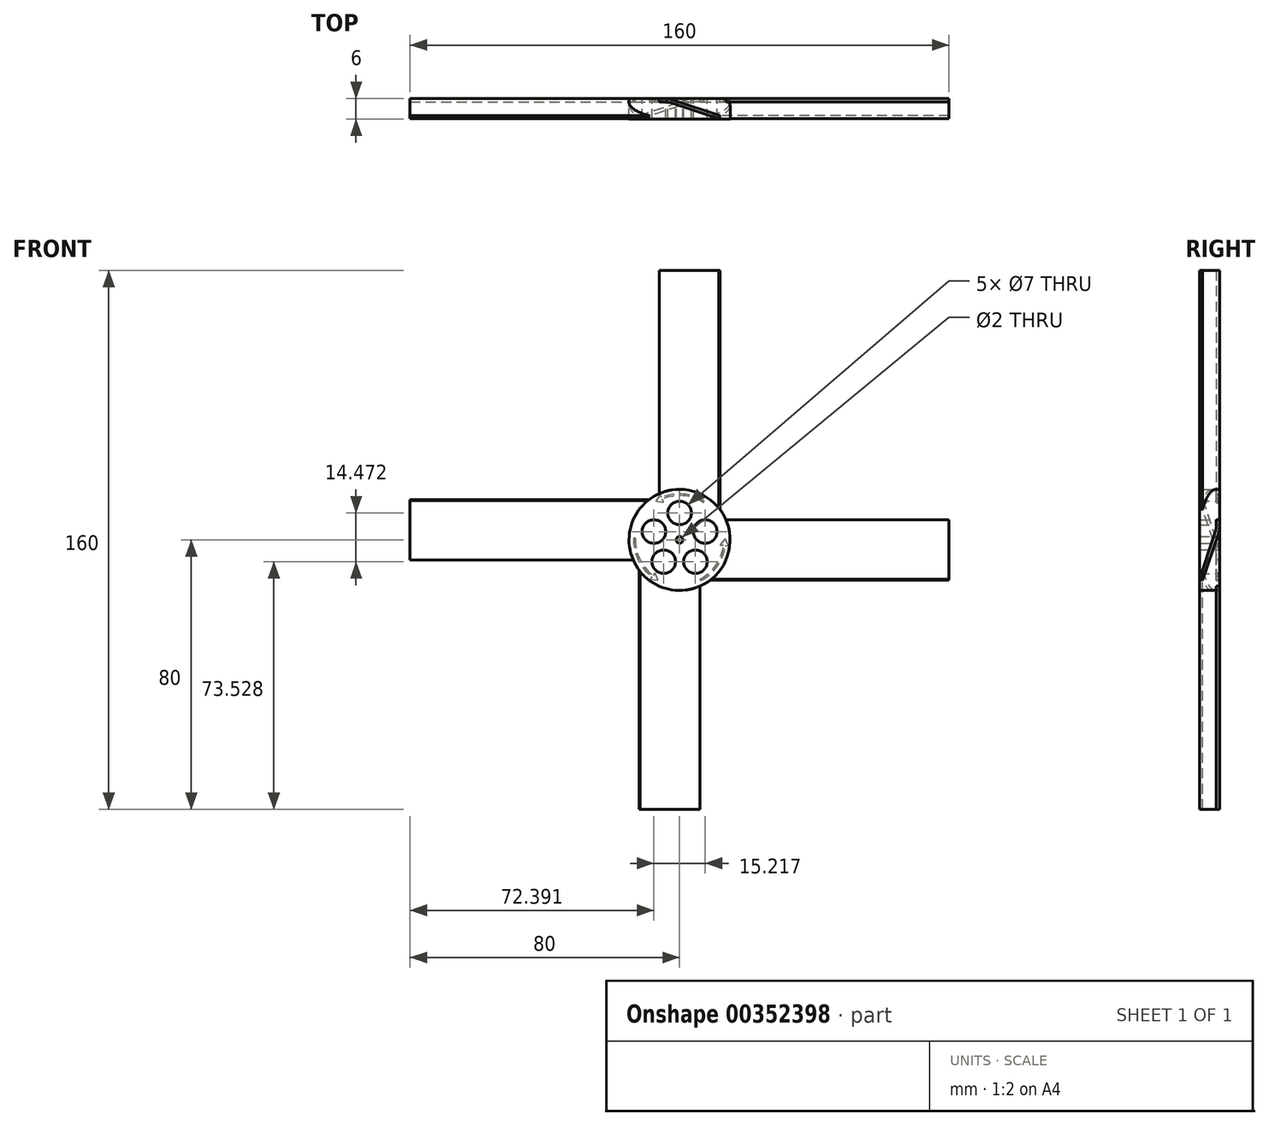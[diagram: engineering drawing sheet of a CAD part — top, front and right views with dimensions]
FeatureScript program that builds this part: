
annotation { "Feature Type Name" : "Feature", "Feature Type Description" : "" }
export const myFeature = defineFeature(function(context is Context, id is Id, definition is map)
    precondition{}
    {
        {
            var Q0;
            Q0=qCreatedBy(makeId("Top.planeOp"),FACE);
            var sketch = newSketch(context, id + "F0", { "sketchPlane" : qUnion([Q0])});
            skLineSegment(sketch, "E0", {"start": v(-3, 0) * mm, "end": v(12, 0) * mm, "construction": true});
            skLineSegment(sketch, "E1", {"start": v(12, 0) * mm, "end": v(12, -5) * mm, "construction": true});
            skLineSegment(sketch, "E2", {"start": v(12, -5) * mm, "end": v(-3, 0) * mm});
            skLineSegment(sketch, "E3.0", {"start": v(11.68, -5.95) * mm, "end": v(-3.32, -0.95) * mm});
            skLineSegment(sketch, "E4", {"start": v(11.68, -5.95) * mm, "end": v(12, -5) * mm});
            skLineSegment(sketch, "E5", {"start": v(-3, 0) * mm, "end": v(-3.32, -0.95) * mm});
            skLineSegment(sketch, "E6", {"start": v(-3, 0) * mm, "end": v(-6, 0) * mm});
            skLineSegment(sketch, "E7", {"start": v(-6, 0) * mm, "end": v(-6, -0.95) * mm});
            skLineSegment(sketch, "E8", {"start": v(-6, -0.95) * mm, "end": v(-3.32, -0.95) * mm});
            skSolve(sketch);
        }
        {
            var Q0;
            Q0=makeQuery(id+"F0.imprint","IMPRINT",FACE,{"disambiguationData":[TD([[makeQuery(id+"F0.imprint","IMPRINT",EDGE,{"derivedFrom":sQuery(id+"F0.wireOp",EDGE,"E2")}),1.0]])]});
            var Q1;
            Q1=makeQuery(id+"F0.imprint","IMPRINT",FACE,{"disambiguationData":[TD([[makeQuery(id+"F0.imprint","IMPRINT",EDGE,{"derivedFrom":sQuery(id+"F0.wireOp",EDGE,"E5")}),-1.0]])]});
            extrude(context, id + "F1", {"entities" : qUnion([Q0, Q1]), "oppositeDirection" : true, "depth" : 80 * mm});
        }
        {
            var Q0;
            Q0=makeQuery(id+"F1.opExtrude","SWEPT_EDGE",EDGE,{"disambiguationData":[OSD([sQuery(id+"F0.wireOp",EDGE,"E3.0"),sQuery(id+"F0.wireOp",EDGE,"E5"),sQuery(id+"F0.wireOp",EDGE,"E8")])]});
            var Q1;
            Q1=makeQuery(id+"F1.opExtrude","SWEPT_EDGE",EDGE,{"disambiguationData":[OSD([sQuery(id+"F0.wireOp",EDGE,"E2"),sQuery(id+"F0.wireOp",EDGE,"E5"),sQuery(id+"F0.wireOp",EDGE,"E6")])]});
            fillet(context, id + "F2", {"entities" : qUnion([Q0, Q1]), "radius" : 7.64 * mm, "tangentPropagation" : true, "allowEdgeOverflow" : false});
        }
        {
            var Q0;
            Q0=qCreatedBy(makeId("Top.planeOp"),FACE);
            var sketch = newSketch(context, id + "F3", { "sketchPlane" : qUnion([Q0])});
            skLineSegment(sketch, "E9", {"start": v(0, 0) * mm, "end": v(0, 27.05) * mm, "construction": true});
            skSolve(sketch);
        }
        {
            var Q0;
            Q0=makeQuery(id+"F1.opExtrude","SWEPT_BODY",BODY,{"disambiguationData":[OSD([sQuery(id+"F0.wireOp",EDGE,"E2"),sQuery(id+"F0.wireOp",EDGE,"E3.0"),sQuery(id+"F0.wireOp",EDGE,"E4"),sQuery(id+"F0.wireOp",EDGE,"E5")])]});
            var Q1;
            Q1=sQuery(id+"F3.wireOp",EDGE,"E9");
            circularPattern(context, id + "F4", {"entities" : qUnion([Q0]), "axis" : qUnion([Q1]), "angle" : 360 * degree, "instanceCount" : 4, "equalSpace" : true});
        }
        {
            var Q0;
            Q0=qCreatedBy(makeId("Front.planeOp"),FACE);
            var sketch = newSketch(context, id + "F5", { "sketchPlane" : qUnion([Q0])});
            skCircle(sketch, "E10", {"center": v(0, 0) * mm, "radius": 15 * mm});
            skSolve(sketch);
        }
        {
            var Q0;
            Q0=makeQuery(id+"F5.imprint","IMPRINT",FACE,{"disambiguationData":[TD([[makeQuery(id+"F5.imprint","IMPRINT",EDGE,{"derivedFrom":sQuery(id+"F5.wireOp",EDGE,"E10")}),1.0]])]});
            extrude(context, id + "F6", {"entities" : qUnion([Q0]), "operationType" : NewBodyOperationType.ADD, "depth" : 6 * mm});
        }
        {
            var Q0;
            Q0=makeQuery(id+"F6.opExtrude","CAP_FACE",FACE,{"disambiguationData":[OSD([sQuery(id+"F5.wireOp",EDGE,"E10")])],"isStart":true});
            var sketch = newSketch(context, id + "F7", { "sketchPlane" : qUnion([Q0])});
            skCircle(sketch, "E11", {"center": v(0, 0) * mm, "radius": 1 * mm});
            skLineSegment(sketch, "E12", {"start": v(0, 0) * mm, "end": v(-1, 0) * mm, "construction": true});
            skCircle(sketch, "E13", {"center": v(0, -8) * mm, "radius": 3.5 * mm});
            skCircle(sketch, "E14.1.0", {"center": v(7.6, -2.47) * mm, "radius": 3.5 * mm});
            skCircle(sketch, "E14.2.0", {"center": v(4.7, 6.47) * mm, "radius": 3.5 * mm});
            skCircle(sketch, "E14.3.0", {"center": v(-4.7, 6.47) * mm, "radius": 3.5 * mm});
            skCircle(sketch, "E14.4.0", {"center": v(-7.6, -2.47) * mm, "radius": 3.5 * mm});
            skSolve(sketch);
        }
        {
            var Q0;
            Q0=makeQuery(id+"F7.imprint","IMPRINT",FACE,{"disambiguationData":[TD([[makeQuery(id+"F7.imprint","IMPRINT",EDGE,{"derivedFrom":sQuery(id+"F7.wireOp",EDGE,"E14.3.0")}),1.0]])]});
            var Q1;
            Q1=makeQuery(id+"F7.imprint","IMPRINT",FACE,{"disambiguationData":[TD([[makeQuery(id+"F7.imprint","IMPRINT",EDGE,{"derivedFrom":sQuery(id+"F7.wireOp",EDGE,"E14.4.0")}),1.0]])]});
            var Q2;
            Q2=makeQuery(id+"F7.imprint","IMPRINT",FACE,{"disambiguationData":[TD([[makeQuery(id+"F7.imprint","IMPRINT",EDGE,{"derivedFrom":sQuery(id+"F7.wireOp",EDGE,"E13")}),1.0]])]});
            var Q3;
            Q3=makeQuery(id+"F7.imprint","IMPRINT",FACE,{"disambiguationData":[TD([[makeQuery(id+"F7.imprint","IMPRINT",EDGE,{"derivedFrom":sQuery(id+"F7.wireOp",EDGE,"E14.1.0")}),1.0]])]});
            var Q4;
            Q4=makeQuery(id+"F7.imprint","IMPRINT",FACE,{"disambiguationData":[TD([[makeQuery(id+"F7.imprint","IMPRINT",EDGE,{"derivedFrom":sQuery(id+"F7.wireOp",EDGE,"E14.2.0")}),1.0]])]});
            var Q5;
            Q5=makeQuery(id+"F7.imprint","IMPRINT",FACE,{"disambiguationData":[TD([[makeQuery(id+"F7.imprint","IMPRINT",EDGE,{"derivedFrom":sQuery(id+"F7.wireOp",EDGE,"E11")}),1.0]])]});
            extrude(context, id + "F8", {"entities" : qUnion([Q0, Q1, Q2, Q3, Q4, Q5]), "operationType" : NewBodyOperationType.REMOVE, "oppositeDirection" : true, "depth" : 25 * mm});
        }
        {
            var Q0;
            Q0=makeQuery(id+"F6.opExtrude","CAP_FACE",FACE,{"disambiguationData":[OSD([sQuery(id+"F5.wireOp",EDGE,"E10")])],"isStart":true});
            var sketch = newSketch(context, id + "F9", { "sketchPlane" : qUnion([Q0])});
            skArc(sketch, "E15", {"start": v(-7.05, -11.11) * mm, "mid": v(-1.07, -13.11) * mm, "end": v(5.16, -12.1) * mm});
            skArc(sketch, "E16.0", {"start": v(-7.29, -11.55) * mm, "mid": v(-1.1, -13.61) * mm, "end": v(5.35, -12.56) * mm});
            skLineSegment(sketch, "E17", {"start": v(-7.05, -11.11) * mm, "end": v(-7.29, -11.55) * mm});
            skLineSegment(sketch, "E18", {"start": v(5.35, -12.56) * mm, "end": v(5.75, -13.48) * mm});
            skLineSegment(sketch, "E19", {"start": v(5.75, -13.48) * mm, "end": v(7.1, -11.55) * mm});
            skLineSegment(sketch, "E20", {"start": v(7.1, -11.55) * mm, "end": v(4.77, -11.18) * mm});
            skLineSegment(sketch, "E21", {"start": v(4.77, -11.18) * mm, "end": v(5.16, -12.1) * mm});
            skLineSegment(sketch, "E22", {"start": v(5.35, -12.56) * mm, "end": v(5.16, -12.1) * mm, "construction": true});
            skLineSegment(sketch, "E23", {"start": v(5.26, -12.33) * mm, "end": v(7.1, -11.55) * mm, "construction": true});
            skLineSegment(sketch, "E24.1.0", {"start": v(6.45, 11.92) * mm, "end": v(7.3, 9.72) * mm});
            skLineSegment(sketch, "E24.1.1", {"start": v(7.3, 9.72) * mm, "end": v(7.9, 10.52) * mm});
            skLineSegment(sketch, "E24.1.2", {"start": v(8.8, 11.72) * mm, "end": v(6.45, 11.92) * mm});
            skArc(sketch, "E24.1.3", {"start": v(13.15, -0.55) * mm, "mid": v(11.9, 5.63) * mm, "end": v(7.9, 10.52) * mm});
            skArc(sketch, "E24.1.4", {"start": v(13.65, -0.54) * mm, "mid": v(12.34, 5.86) * mm, "end": v(8.2, 10.92) * mm});
            skLineSegment(sketch, "E24.1.5", {"start": v(8.2, 10.92) * mm, "end": v(8.8, 11.72) * mm});
            skLineSegment(sketch, "E24.1.6", {"start": v(8.05, 10.72) * mm, "end": v(6.45, 11.92) * mm, "construction": true});
            skLineSegment(sketch, "E24.1.7", {"start": v(13.15, -0.55) * mm, "end": v(13.65, -0.54) * mm});
            skLineSegment(sketch, "E24.1.8", {"start": v(8.2, 10.92) * mm, "end": v(7.9, 10.52) * mm, "construction": true});
            skLineSegment(sketch, "E24.2.0", {"start": v(-13.55, -0.37) * mm, "end": v(-12.07, 1.46) * mm});
            skLineSegment(sketch, "E24.2.1", {"start": v(-12.07, 1.46) * mm, "end": v(-13.06, 1.58) * mm});
            skLineSegment(sketch, "E24.2.2", {"start": v(-14.55, 1.77) * mm, "end": v(-13.55, -0.37) * mm});
            skArc(sketch, "E24.2.3", {"start": v(-6.1, 11.66) * mm, "mid": v(-10.82, 7.48) * mm, "end": v(-13.06, 1.58) * mm});
            skArc(sketch, "E24.2.4", {"start": v(-6.36, 12.09) * mm, "mid": v(-11.24, 7.75) * mm, "end": v(-13.56, 1.64) * mm});
            skLineSegment(sketch, "E24.2.5", {"start": v(-13.56, 1.64) * mm, "end": v(-14.55, 1.77) * mm});
            skLineSegment(sketch, "E24.2.6", {"start": v(-13.3, 1.61) * mm, "end": v(-13.55, -0.37) * mm, "construction": true});
            skLineSegment(sketch, "E24.2.7", {"start": v(-6.1, 11.66) * mm, "end": v(-6.36, 12.09) * mm});
            skLineSegment(sketch, "E24.2.8", {"start": v(-13.56, 1.64) * mm, "end": v(-13.06, 1.58) * mm, "construction": true});
            skSolve(sketch);
        }
        {
            var Q0;
            Q0=makeQuery(id+"F9.imprint","IMPRINT",FACE,{"disambiguationData":[TD([[makeQuery(id+"F9.imprint","IMPRINT",EDGE,{"derivedFrom":sQuery(id+"F9.wireOp",EDGE,"E15")}),-1.0]])]});
            var Q1;
            Q1=makeQuery(id+"F9.imprint","IMPRINT",FACE,{"disambiguationData":[TD([[makeQuery(id+"F9.imprint","IMPRINT",EDGE,{"derivedFrom":sQuery(id+"F9.wireOp",EDGE,"E24.1.0")}),1.0]])]});
            var Q2;
            Q2=makeQuery(id+"F9.imprint","IMPRINT",FACE,{"disambiguationData":[TD([[makeQuery(id+"F9.imprint","IMPRINT",EDGE,{"derivedFrom":sQuery(id+"F9.wireOp",EDGE,"E24.2.0")}),1.0]])]});
            extrude(context, id + "F10", {"entities" : qUnion([Q0, Q1, Q2]), "operationType" : NewBodyOperationType.REMOVE, "oppositeDirection" : true, "depth" : 1 * mm});
        }
        {
            var Q0;
            Q0=makeQuery(id+"F1.opExtrude","SWEPT_BODY",BODY,{"disambiguationData":[OSD([sQuery(id+"F0.wireOp",EDGE,"E2"),sQuery(id+"F0.wireOp",EDGE,"E3.0"),sQuery(id+"F0.wireOp",EDGE,"E4"),sQuery(id+"F0.wireOp",EDGE,"E6"),sQuery(id+"F0.wireOp",EDGE,"E7"),sQuery(id+"F0.wireOp",EDGE,"E8")])]});
            var Q1;
            Q1=qCreatedBy(makeId("Top.planeOp"),FACE);
            mirror(context, id + "F11", {"entities" : qUnion([Q0]), "mirrorPlane" : qUnion([Q1])});
        }
        {
            var Q0;
            Q0=makeQuery(id+"F1.opExtrude","SWEPT_BODY",BODY,{"disambiguationData":[OSD([sQuery(id+"F0.wireOp",EDGE,"E2"),sQuery(id+"F0.wireOp",EDGE,"E3.0"),sQuery(id+"F0.wireOp",EDGE,"E4"),sQuery(id+"F0.wireOp",EDGE,"E6"),sQuery(id+"F0.wireOp",EDGE,"E7"),sQuery(id+"F0.wireOp",EDGE,"E8")])]});
            deleteBodies(context, id + "F12", {"entities" : qUnion([Q0])});
        }
    });
